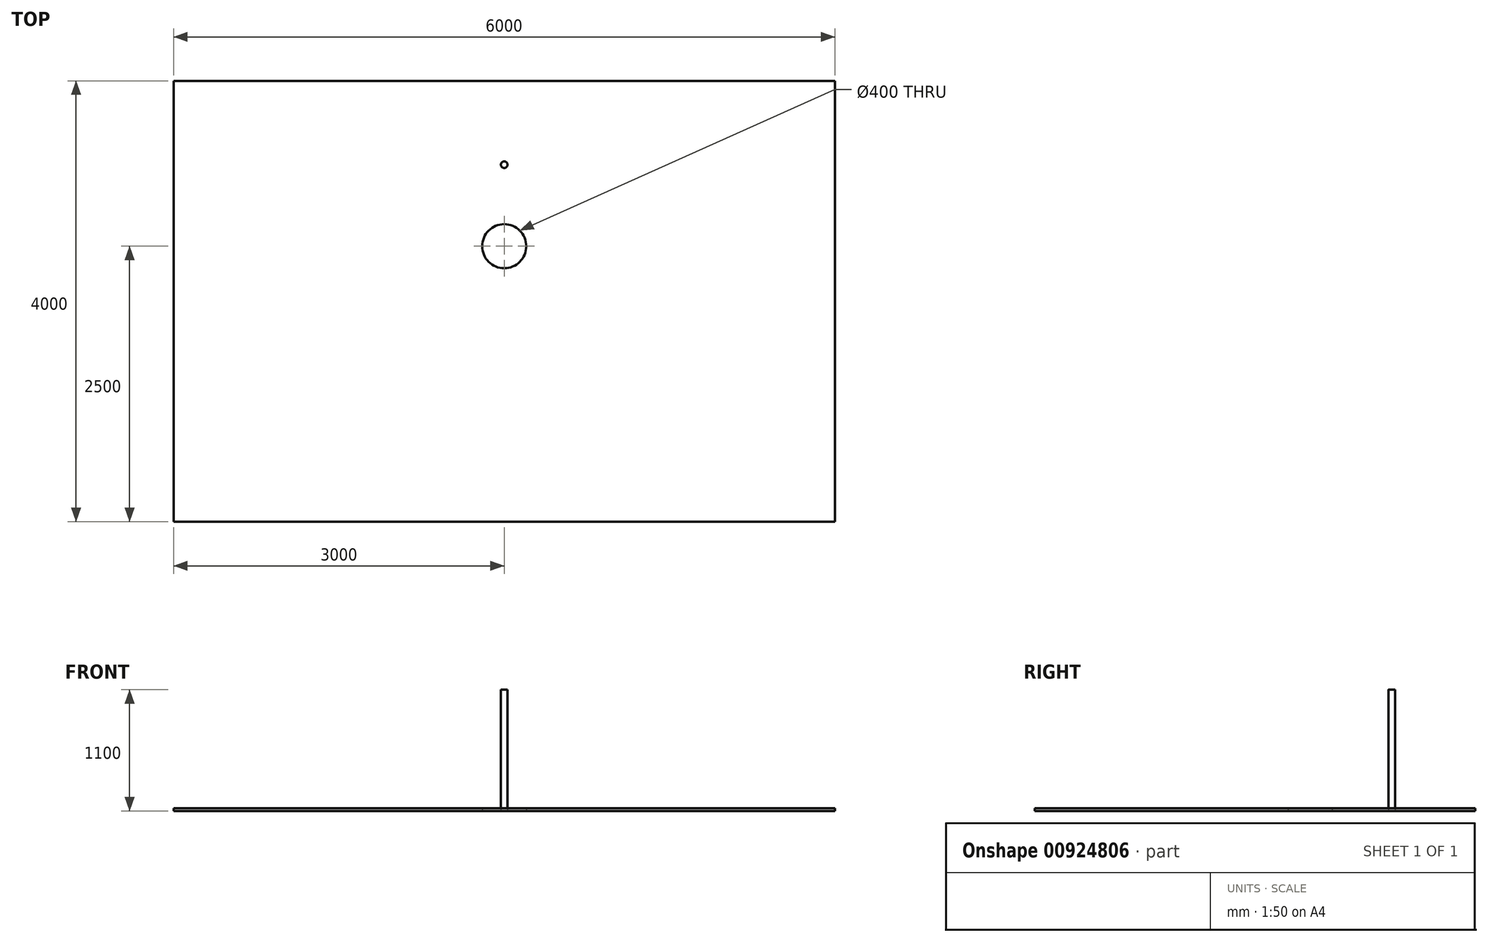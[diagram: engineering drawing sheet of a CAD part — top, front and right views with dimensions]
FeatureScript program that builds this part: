
annotation { "Feature Type Name" : "Feature", "Feature Type Description" : "" }
export const myFeature = defineFeature(function(context is Context, id is Id, definition is map)
    precondition{}
    {
        {
            var Q0;
            Q0=qCreatedBy(makeId("Top.planeOp"),FACE);
            var sketch = newSketch(context, id + "F0", { "sketchPlane" : qUnion([Q0])});
            skLineSegment(sketch, "E0.bottom", {"start": v(-3000, -3300) * mm, "end": v(3000, -3300) * mm});
            skLineSegment(sketch, "E0.top", {"start": v(-3000, 700) * mm, "end": v(3000, 700) * mm});
            skLineSegment(sketch, "E0.left", {"start": v(-3000, -3300) * mm, "end": v(-3000, 700) * mm});
            skLineSegment(sketch, "E0.right", {"start": v(3000, -3300) * mm, "end": v(3000, 700) * mm});
            skCircle(sketch, "E1", {"center": v(0, -800) * mm, "radius": 200 * mm});
            skSolve(sketch);
        }
        {
            var Q0;
            Q0=qSketchRegion(id+"F0",true);
            extrude(context, id + "F1", {"entities" : qUnion([Q0]), "depth" : 25 * mm, "offsetDistance" : 25 * mm});
        }
        {
            var Q0;
            Q0=makeQuery(id+"F0.imprint","IMPRINT",FACE,{"disambiguationData":[TD([[makeQuery(id+"F0.imprint","IMPRINT",EDGE,{"derivedFrom":sQuery(id+"F0.wireOp",EDGE,"E0.bottom")}),1.0]])]});
            var sketch = newSketch(context, id + "F2", { "sketchPlane" : qUnion([Q0])});
            skCircle(sketch, "E2", {"center": v(0, -60) * mm, "radius": 30 * mm});
            skSolve(sketch);
        }
        {
            var Q0;
            Q0=qSketchRegion(id+"F2",true);
            extrude(context, id + "F3", {"entities" : qUnion([Q0]), "depth" : 1100 * mm, "offsetDistance" : 25 * mm});
        }
    });
